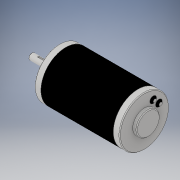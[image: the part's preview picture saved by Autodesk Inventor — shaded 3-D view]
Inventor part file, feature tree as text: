
AUTODESK INVENTOR PART (.ipt)
format: ipt  version: 2018 (Build 220112000, 112)  size: 168,448 bytes
history: native  units: in
note: dims shown in document units (in); Inventor stores cm internally (conversion verified against a paired STEP export)
features: chamfer x1
ambient origin geometry x8: Origin, YZ Plane, XZ Plane, XY Plane, X Axis, Y Axis, Z Axis, Center Point
bodies: Solid1 (feature_tree)
feature tree (1):
  chamfer  "Chamfer3"  [1 undecoded]
note: 1 required parameter value undecoded (feature->parameter linkage not recoverable at this tier; creation-order binding heuristic only, values carry confidence <= 0.55)
